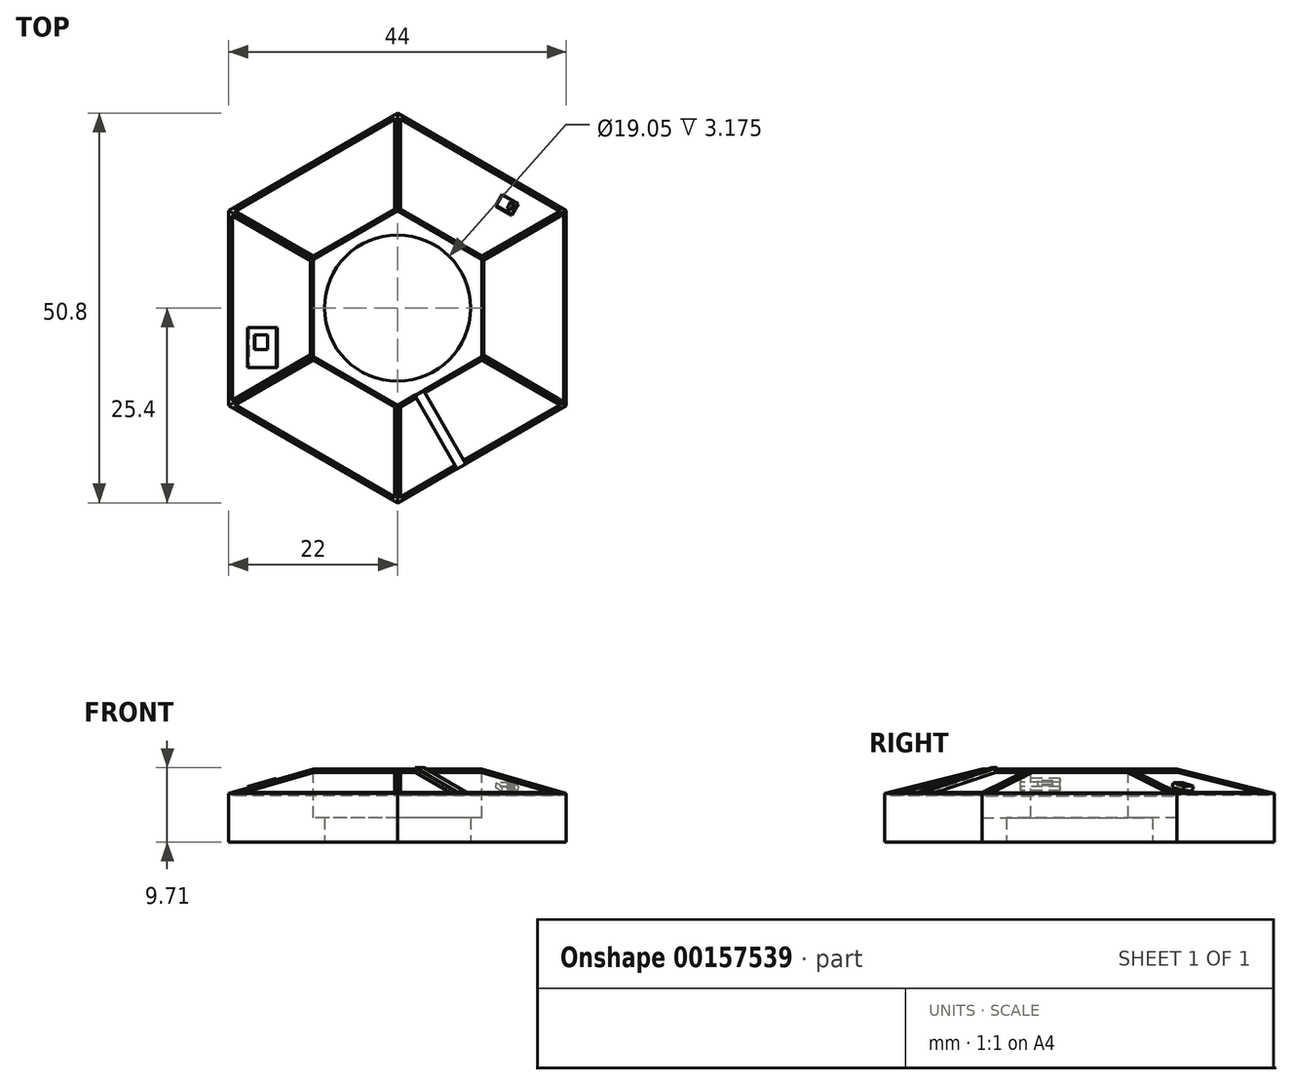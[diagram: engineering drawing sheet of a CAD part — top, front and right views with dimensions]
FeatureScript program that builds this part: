
annotation { "Feature Type Name" : "Feature", "Feature Type Description" : "" }
export const myFeature = defineFeature(function(context is Context, id is Id, definition is map)
    precondition{}
    {
        {
            var Q0;
            Q0=qCreatedBy(makeId("Top.planeOp"),FACE);
            var sketch = newSketch(context, id + "F0", { "sketchPlane" : qUnion([Q0])});
            skCircle(sketch, "E0.cCircle", {"center": v(0, 0) * mm, "radius": 25.4 * mm, "construction": true});
            skLineSegment(sketch, "E0.0", {"start": v(0, 25.4) * mm, "end": v(22, 12.7) * mm});
            skLineSegment(sketch, "E0.1", {"start": v(22, 12.7) * mm, "end": v(22, -12.7) * mm});
            skLineSegment(sketch, "E0.2", {"start": v(22, -12.7) * mm, "end": v(0, -25.4) * mm});
            skLineSegment(sketch, "E0.3", {"start": v(0, -25.4) * mm, "end": v(-22, -12.7) * mm});
            skLineSegment(sketch, "E0.4", {"start": v(-22, -12.7) * mm, "end": v(-22, 12.7) * mm});
            skLineSegment(sketch, "E0.5", {"start": v(-22, 12.7) * mm, "end": v(0, 25.4) * mm});
            skCircle(sketch, "E1.cCircle", {"center": v(0, 0) * mm, "radius": 12.7 * mm, "construction": true});
            skLineSegment(sketch, "E1.0", {"start": v(0, 12.7) * mm, "end": v(11, 6.35) * mm});
            skLineSegment(sketch, "E1.1", {"start": v(11, 6.35) * mm, "end": v(11, -6.35) * mm});
            skLineSegment(sketch, "E1.2", {"start": v(11, -6.35) * mm, "end": v(0, -12.7) * mm});
            skLineSegment(sketch, "E1.3", {"start": v(0, -12.7) * mm, "end": v(-11, -6.35) * mm});
            skLineSegment(sketch, "E1.4", {"start": v(-11, -6.35) * mm, "end": v(-11, 6.35) * mm});
            skLineSegment(sketch, "E1.5", {"start": v(-11, 6.35) * mm, "end": v(0, 12.7) * mm});
            skCircle(sketch, "E2", {"center": v(0, 0) * mm, "radius": 9.53 * mm});
            skSolve(sketch);
        }
        {
            var Q0;
            Q0=makeQuery(id+"F0.imprint","IMPRINT",FACE,{"disambiguationData":[TD([[makeQuery(id+"F0.imprint","IMPRINT",EDGE,{"derivedFrom":sQuery(id+"F0.wireOp",EDGE,"E0.0")}),-1.0]])]});
            var Q1;
            {var subQ0=sQuery(id+"F0.wireOp",EDGE,"Us5ljXmE-I7RQ-zfye-zbqb-6XDtsWbHNBCU");var subQ4=makeQuery(id+"F0.imprint","INTERSECT",VERTEX,{"derivedFrom":[sQuery(id+"F0.wireOp",EDGE,"E1.0"),subQ0]});Q1=makeQuery(id+"F0.imprint","IMPRINT",FACE,{"disambiguationData":[TD([[makeQuery(id+"F0.imprint","IMPRINT",EDGE,{"disambiguationData":[TD([[subQ4,1.0]])],"derivedFrom":subQ0}),1.0]])]});}
            var Q2;
            {var subQ0=sQuery(id+"F0.wireOp",EDGE,"E1.1");var subQ1=sQuery(id+"F0.wireOp",EDGE,"E1.0");var subQ2=makeQuery(id+"F0.imprint","INTERSECT",VERTEX,{"derivedFrom":[subQ1,subQ0]});Q2=makeQuery(id+"F0.imprint","IMPRINT",FACE,{"disambiguationData":[TD([[makeQuery(id+"F0.imprint","IMPRINT",EDGE,{"disambiguationData":[TD([[subQ2,1.0]])],"derivedFrom":subQ1}),-1.0]])]});}
            var Q3;
            {var subQ0=sQuery(id+"F0.wireOp",EDGE,"E1.2");var subQ1=sQuery(id+"F0.wireOp",EDGE,"E1.1");var subQ2=makeQuery(id+"F0.imprint","INTERSECT",VERTEX,{"derivedFrom":[subQ1,subQ0]});Q3=makeQuery(id+"F0.imprint","IMPRINT",FACE,{"disambiguationData":[TD([[makeQuery(id+"F0.imprint","IMPRINT",EDGE,{"disambiguationData":[TD([[subQ2,1.0]])],"derivedFrom":subQ1}),-1.0]])]});}
            var Q4;
            {var subQ0=sQuery(id+"F0.wireOp",EDGE,"E1.3");var subQ1=sQuery(id+"F0.wireOp",EDGE,"E1.2");var subQ2=makeQuery(id+"F0.imprint","INTERSECT",VERTEX,{"derivedFrom":[subQ1,subQ0]});Q4=makeQuery(id+"F0.imprint","IMPRINT",FACE,{"disambiguationData":[TD([[makeQuery(id+"F0.imprint","IMPRINT",EDGE,{"disambiguationData":[TD([[subQ2,1.0]])],"derivedFrom":subQ1}),-1.0]])]});}
            var Q5;
            {var subQ0=sQuery(id+"F0.wireOp",EDGE,"E1.4");var subQ1=sQuery(id+"F0.wireOp",EDGE,"E1.3");var subQ2=makeQuery(id+"F0.imprint","INTERSECT",VERTEX,{"derivedFrom":[subQ1,subQ0]});Q5=makeQuery(id+"F0.imprint","IMPRINT",FACE,{"disambiguationData":[TD([[makeQuery(id+"F0.imprint","IMPRINT",EDGE,{"disambiguationData":[TD([[subQ2,1.0]])],"derivedFrom":subQ1}),-1.0]])]});}
            var Q6;
            {var subQ0=sQuery(id+"F0.wireOp",EDGE,"E1.5");var subQ1=sQuery(id+"F0.wireOp",EDGE,"E1.4");var subQ2=makeQuery(id+"F0.imprint","INTERSECT",VERTEX,{"derivedFrom":[subQ1,subQ0]});Q6=makeQuery(id+"F0.imprint","IMPRINT",FACE,{"disambiguationData":[TD([[makeQuery(id+"F0.imprint","IMPRINT",EDGE,{"disambiguationData":[TD([[subQ2,1.0]])],"derivedFrom":subQ1}),-1.0]])]});}
            var Q7;
            {var subQ0=sQuery(id+"F0.wireOp",EDGE,"E1.5");var subQ1=sQuery(id+"F0.wireOp",EDGE,"E1.0");var subQ2=makeQuery(id+"F0.imprint","INTERSECT",VERTEX,{"derivedFrom":[subQ1,subQ0]});Q7=makeQuery(id+"F0.imprint","IMPRINT",FACE,{"disambiguationData":[TD([[makeQuery(id+"F0.imprint","IMPRINT",EDGE,{"disambiguationData":[TD([[subQ2,-1.0]])],"derivedFrom":subQ1}),-1.0]])]});}
            extrude(context, id + "F1", {"entities" : qUnion([Q0, Q1, Q2, Q3, Q4, Q5, Q6, Q7]), "depth" : 6.35 * mm});
        }
        {
            var Q0;
            Q0=makeQuery(id+"F1.opExtrude","CAP_FACE",FACE,{"disambiguationData":[OSD([sQuery(id+"F0.wireOp",EDGE,"E0.0"),sQuery(id+"F0.wireOp",EDGE,"E0.1"),sQuery(id+"F0.wireOp",EDGE,"E0.2"),sQuery(id+"F0.wireOp",EDGE,"E0.3"),sQuery(id+"F0.wireOp",EDGE,"E0.4"),sQuery(id+"F0.wireOp",EDGE,"E0.5")])],"isStart":false});
            var sketch = newSketch(context, id + "F2", { "sketchPlane" : qUnion([Q0])});
            skLineSegment(sketch, "E3.0", {"start": v(-11, -6.35) * mm, "end": v(-11, 6.35) * mm});
            skLineSegment(sketch, "E3.1", {"start": v(0, -12.7) * mm, "end": v(-11, -6.35) * mm});
            skLineSegment(sketch, "E3.2", {"start": v(11, -6.35) * mm, "end": v(0, -12.7) * mm});
            skLineSegment(sketch, "E3.3", {"start": v(11, 6.35) * mm, "end": v(11, -6.35) * mm});
            skLineSegment(sketch, "E3.4", {"start": v(0, 12.7) * mm, "end": v(11, 6.35) * mm});
            skLineSegment(sketch, "E3.5", {"start": v(-11, 6.35) * mm, "end": v(0, 12.7) * mm});
            skSolve(sketch);
        }
        {
            var Q0;
            Q0=makeQuery(id+"F2.imprint","IMPRINT",FACE,{"disambiguationData":[TD([[makeQuery(id+"F2.imprint","IMPRINT",EDGE,{"derivedFrom":sQuery(id+"F2.wireOp",EDGE,"E3.0")}),-1.0]])]});
            extrude(context, id + "F3", {"entities" : qUnion([Q0]), "operationType" : NewBodyOperationType.ADD, "depth" : 3.17 * mm});
        }
        {
            var Q0;
            Q0=makeQuery(id+"F2.imprint","IMPRINT",FACE,{"disambiguationData":[TD([[makeQuery(id+"F2.imprint","IMPRINT",EDGE,{"derivedFrom":sQuery(id+"F2.wireOp",EDGE,"E3.0")}),1.0]])]});
            var sketch = newSketch(context, id + "F4", { "sketchPlane" : qUnion([Q0])});
            skLineSegment(sketch, "E4.0", {"start": v(22, -12.7) * mm, "end": v(0, -25.4) * mm});
            skLineSegment(sketch, "E4.1", {"start": v(0, -25.4) * mm, "end": v(-22, -12.7) * mm});
            skLineSegment(sketch, "E4.2", {"start": v(-22, -12.7) * mm, "end": v(-22, 12.7) * mm});
            skLineSegment(sketch, "E4.3", {"start": v(-22, 12.7) * mm, "end": v(0, 25.4) * mm});
            skLineSegment(sketch, "E4.4", {"start": v(0, 25.4) * mm, "end": v(22, 12.7) * mm});
            skLineSegment(sketch, "E4.5", {"start": v(22, 12.7) * mm, "end": v(22, -12.7) * mm});
            skSolve(sketch);
        }
        {
            var Q0;
            Q0=makeQuery(id+"F3.opExtrude","CAP_FACE",FACE,{"disambiguationData":[OSD([sQuery(id+"F2.wireOp",EDGE,"E3.0"),sQuery(id+"F2.wireOp",EDGE,"E3.1"),sQuery(id+"F2.wireOp",EDGE,"E3.2"),sQuery(id+"F2.wireOp",EDGE,"E3.3"),sQuery(id+"F2.wireOp",EDGE,"E3.4"),sQuery(id+"F2.wireOp",EDGE,"E3.5")])],"isStart":false});
            var sketch = newSketch(context, id + "F5", { "sketchPlane" : qUnion([Q0])});
            skLineSegment(sketch, "E5.0", {"start": v(11, -6.35) * mm, "end": v(0, -12.7) * mm});
            skLineSegment(sketch, "E5.1", {"start": v(0, -12.7) * mm, "end": v(-11, -6.35) * mm});
            skLineSegment(sketch, "E5.2", {"start": v(-11, -6.35) * mm, "end": v(-11, 6.35) * mm});
            skLineSegment(sketch, "E5.3", {"start": v(-11, 6.35) * mm, "end": v(0, 12.7) * mm});
            skLineSegment(sketch, "E5.4", {"start": v(0, 12.7) * mm, "end": v(11, 6.35) * mm});
            skLineSegment(sketch, "E5.5", {"start": v(11, 6.35) * mm, "end": v(11, -6.35) * mm});
            skSolve(sketch);
        }
        {
            var Q1;
            Q1 = qSketchRegion(id + "F4", true);
            var Q2;
            Q2 = qSketchRegion(id + "F5", true);
            loft(context, id + "F6", {"operationType" : NewBodyOperationType.ADD, "sheetProfilesArray" : [{ "sheetProfileEntities" : qUnion([Q1]) }, { "sheetProfileEntities" : qUnion([Q2]) }]});
        }
        {
            var Q0;
            Q0=makeQuery(id+"F6.opLoft","SWEPT_FACE",FACE,{"disambiguationData":[OSD([sQuery(id+"F4.wireOp",EDGE,"E4.0"),sQuery(id+"F4.wireOp",EDGE,"E4.4"),sQuery(id+"F4.wireOp",EDGE,"E4.5"),sQuery(id+"F5.wireOp",EDGE,"E5.0"),sQuery(id+"F5.wireOp",EDGE,"E5.4"),sQuery(id+"F5.wireOp",EDGE,"E5.5")])]});
            var sketch = newSketch(context, id + "F7", { "sketchPlane" : qUnion([Q0])});
            skLineSegment(sketch, "E6.0.0", {"start": v(19.37, 12.7) * mm, "end": v(7.93, 6.35) * mm});
            skLineSegment(sketch, "E6.0.1", {"start": v(7.93, 6.35) * mm, "end": v(7.93, -6.35) * mm});
            skLineSegment(sketch, "E6.0.2", {"start": v(7.93, -6.35) * mm, "end": v(19.37, -12.7) * mm});
            skLineSegment(sketch, "E6.0.3", {"start": v(19.37, -12.7) * mm, "end": v(19.37, 12.7) * mm});
            skLineSegment(sketch, "E7.0", {"start": v(8.18, -6.2) * mm, "end": v(19.12, -12.27) * mm});
            skLineSegment(sketch, "E7.1", {"start": v(8.18, 6.2) * mm, "end": v(8.18, -6.2) * mm});
            skLineSegment(sketch, "E7.2", {"start": v(19.12, 12.27) * mm, "end": v(8.18, 6.2) * mm});
            skLineSegment(sketch, "E7.3", {"start": v(19.12, -12.27) * mm, "end": v(19.12, 12.27) * mm});
            skSolve(sketch);
        }
        {
            var Q0;
            Q0=makeQuery(id+"F3.opExtrude","CAP_FACE",FACE,{"disambiguationData":[OSD([sQuery(id+"F2.wireOp",EDGE,"E3.0"),sQuery(id+"F2.wireOp",EDGE,"E3.1"),sQuery(id+"F2.wireOp",EDGE,"E3.2"),sQuery(id+"F2.wireOp",EDGE,"E3.3"),sQuery(id+"F2.wireOp",EDGE,"E3.4"),sQuery(id+"F2.wireOp",EDGE,"E3.5")])],"isStart":false});
            var Q1;
            Q1=sQuery(id+"F0.wireOp",EDGE,"E1.3");
            var Q2;
            Q2=sQuery(id+"F0.wireOp",EDGE,"E1.2");
            var Q3;
            Q3=sQuery(id+"F0.wireOp",EDGE,"E1.1");
            var Q4;
            Q4=sQuery(id+"F0.wireOp",EDGE,"E1.0");
            var Q5;
            Q5=sQuery(id+"F0.wireOp",EDGE,"E1.5");
            var Q6;
            Q6=sQuery(id+"F0.wireOp",EDGE,"E1.4");
            extrude(context, id + "F8", {"entities" : qUnion([Q0]), "operationType" : NewBodyOperationType.REMOVE, "surfaceEntities" : qUnion([Q1, Q2, Q3, Q4, Q5, Q6]), "oppositeDirection" : true, "depth" : 6.35 * mm});
        }
        {
            var Q0;
            Q0=makeQuery(id+"F6.opLoft","SWEPT_FACE",FACE,{"disambiguationData":[OSD([sQuery(id+"F4.wireOp",EDGE,"E4.1"),sQuery(id+"F4.wireOp",EDGE,"E4.2"),sQuery(id+"F4.wireOp",EDGE,"E4.3"),sQuery(id+"F5.wireOp",EDGE,"E5.1"),sQuery(id+"F5.wireOp",EDGE,"E5.2"),sQuery(id+"F5.wireOp",EDGE,"E5.3")])]});
            var sketch = newSketch(context, id + "F9", { "sketchPlane" : qUnion([Q0])});
            skLineSegment(sketch, "E8.bottom", {"start": v(-16.76, -2.55) * mm, "end": v(-12.87, -2.55) * mm});
            skLineSegment(sketch, "E8.top", {"start": v(-16.76, -7.73) * mm, "end": v(-12.87, -7.73) * mm});
            skLineSegment(sketch, "E8.left", {"start": v(-16.76, -2.55) * mm, "end": v(-16.76, -7.73) * mm});
            skLineSegment(sketch, "E8.right", {"start": v(-12.87, -2.55) * mm, "end": v(-12.87, -7.73) * mm});
            skLineSegment(sketch, "E9.bottom", {"start": v(-15.8, -3.5) * mm, "end": v(-14.08, -3.5) * mm});
            skLineSegment(sketch, "E9.top", {"start": v(-15.8, -5.4) * mm, "end": v(-14.08, -5.4) * mm});
            skLineSegment(sketch, "E9.left", {"start": v(-15.8, -3.5) * mm, "end": v(-15.8, -5.4) * mm});
            skLineSegment(sketch, "E9.right", {"start": v(-14.08, -3.5) * mm, "end": v(-14.08, -5.4) * mm});
            skSolve(sketch);
        }
        {
            var Q0;
            Q0=makeQuery(id+"F9.imprint","IMPRINT",FACE,{"disambiguationData":[TD([[makeQuery(id+"F9.imprint","IMPRINT",EDGE,{"derivedFrom":sQuery(id+"F9.wireOp",EDGE,"E8.bottom")}),-1.0]])]});
            extrude(context, id + "F10", {"entities" : qUnion([Q0]), "operationType" : NewBodyOperationType.ADD, "depth" : 0.2 * mm});
        }
        {
            var Q0;
            Q0=makeQuery(id+"F6.opLoft","SWEPT_FACE",FACE,{"disambiguationData":[OSD([sQuery(id+"F4.wireOp",EDGE,"E4.0"),sQuery(id+"F4.wireOp",EDGE,"E4.1"),sQuery(id+"F4.wireOp",EDGE,"E4.5"),sQuery(id+"F5.wireOp",EDGE,"E5.0"),sQuery(id+"F5.wireOp",EDGE,"E5.1"),sQuery(id+"F5.wireOp",EDGE,"E5.5")])]});
            var sketch = newSketch(context, id + "F11", { "sketchPlane" : qUnion([Q0])});
            skLineSegment(sketch, "E10", {"start": v(0.55, -8.76) * mm, "end": v(6.1, -18.77) * mm});
            skLineSegment(sketch, "E11", {"start": v(6.1, -18.77) * mm, "end": v(7.28, -18.11) * mm});
            skLineSegment(sketch, "E12", {"start": v(7.28, -18.11) * mm, "end": v(1.73, -8.1) * mm});
            skLineSegment(sketch, "E13", {"start": v(1.73, -8.1) * mm, "end": v(0.55, -8.76) * mm});
            skSolve(sketch);
        }
        {
            var Q0;
            Q0=makeQuery(id+"F11.imprint","IMPRINT",FACE,{"disambiguationData":[TD([[makeQuery(id+"F11.imprint","IMPRINT",EDGE,{"derivedFrom":sQuery(id+"F11.wireOp",EDGE,"E10")}),1.0]])]});
            extrude(context, id + "F12", {"entities" : qUnion([Q0]), "operationType" : NewBodyOperationType.ADD, "depth" : 0.2 * mm});
        }
        {
            var Q0;
            Q0=makeQuery(id+"F7.imprint","IMPRINT",FACE,{"disambiguationData":[TD([[makeQuery(id+"F7.imprint","IMPRINT",EDGE,{"derivedFrom":sQuery(id+"F7.wireOp",EDGE,"E7.0")}),1.0]])]});
            extrude(context, id + "F13", {"entities" : qUnion([Q0]), "operationType" : NewBodyOperationType.REMOVE, "oppositeDirection" : true, "depth" : 0.38 * mm});
        }
        {
            var Q0;
            Q0=makeQuery(id+"F6.opLoft","SWEPT_FACE",FACE,{"disambiguationData":[OSD([sQuery(id+"F4.wireOp",EDGE,"E4.3"),sQuery(id+"F4.wireOp",EDGE,"E4.4"),sQuery(id+"F4.wireOp",EDGE,"E4.5"),sQuery(id+"F5.wireOp",EDGE,"E5.3"),sQuery(id+"F5.wireOp",EDGE,"E5.4"),sQuery(id+"F5.wireOp",EDGE,"E5.5")])]});
            var sketch = newSketch(context, id + "F14", { "sketchPlane" : qUnion([Q0])});
            skLineSegment(sketch, "E14.0", {"start": v(-1.7, 23.1) * mm, "end": v(-1.7, 10.01) * mm});
            skLineSegment(sketch, "E14.1", {"start": v(-1.7, 10.01) * mm, "end": v(9.4, 3.85) * mm});
            skLineSegment(sketch, "E14.2", {"start": v(20.5, 10.78) * mm, "end": v(9.4, 3.85) * mm});
            skLineSegment(sketch, "E14.3", {"start": v(-1.7, 23.1) * mm, "end": v(20.5, 10.78) * mm});
            skLineSegment(sketch, "E15.0", {"start": v(-1.33, 10.24) * mm, "end": v(9.39, 4.3) * mm});
            skLineSegment(sketch, "E15.1", {"start": v(-1.33, 22.45) * mm, "end": v(-1.33, 10.24) * mm});
            skLineSegment(sketch, "E15.2", {"start": v(-1.33, 22.45) * mm, "end": v(19.75, 10.76) * mm});
            skLineSegment(sketch, "E15.3", {"start": v(19.75, 10.76) * mm, "end": v(9.39, 4.3) * mm});
            skSolve(sketch);
        }
        {
            var Q0;
            Q0=makeQuery(id+"F14.imprint","IMPRINT",FACE,{"disambiguationData":[TD([[makeQuery(id+"F14.imprint","IMPRINT",EDGE,{"derivedFrom":sQuery(id+"F14.wireOp",EDGE,"E15.0")}),1.0]])]});
            extrude(context, id + "F15", {"entities" : qUnion([Q0]), "operationType" : NewBodyOperationType.REMOVE, "oppositeDirection" : true, "depth" : 0.38 * mm});
        }
        {
            var Q0;
            Q0=makeQuery(id+"F6.opLoft","SWEPT_FACE",FACE,{"disambiguationData":[OSD([sQuery(id+"F4.wireOp",EDGE,"E4.2"),sQuery(id+"F4.wireOp",EDGE,"E4.3"),sQuery(id+"F4.wireOp",EDGE,"E4.4"),sQuery(id+"F5.wireOp",EDGE,"E5.2"),sQuery(id+"F5.wireOp",EDGE,"E5.3"),sQuery(id+"F5.wireOp",EDGE,"E5.4")])]});
            var sketch = newSketch(context, id + "F16", { "sketchPlane" : qUnion([Q0])});
            skLineSegment(sketch, "E16.0", {"start": v(-9.4, 3.85) * mm, "end": v(1.7, 10.01) * mm});
            skLineSegment(sketch, "E16.1", {"start": v(1.7, 23.1) * mm, "end": v(1.7, 10.01) * mm});
            skLineSegment(sketch, "E16.2", {"start": v(-20.5, 10.78) * mm, "end": v(1.7, 23.1) * mm});
            skLineSegment(sketch, "E16.3", {"start": v(-20.5, 10.78) * mm, "end": v(-9.4, 3.85) * mm});
            skLineSegment(sketch, "E17.0", {"start": v(-9.39, 4.3) * mm, "end": v(1.33, 10.24) * mm});
            skLineSegment(sketch, "E17.1", {"start": v(-19.75, 10.76) * mm, "end": v(-9.39, 4.3) * mm});
            skLineSegment(sketch, "E17.2", {"start": v(-19.75, 10.76) * mm, "end": v(1.33, 22.45) * mm});
            skLineSegment(sketch, "E17.3", {"start": v(1.33, 22.45) * mm, "end": v(1.33, 10.24) * mm});
            skSolve(sketch);
        }
        {
            var Q0;
            Q0=makeQuery(id+"F16.imprint","IMPRINT",FACE,{"disambiguationData":[TD([[makeQuery(id+"F16.imprint","IMPRINT",EDGE,{"derivedFrom":sQuery(id+"F16.wireOp",EDGE,"E17.0")}),1.0]])]});
            extrude(context, id + "F17", {"entities" : qUnion([Q0]), "operationType" : NewBodyOperationType.REMOVE, "oppositeDirection" : true, "depth" : 0.38 * mm});
        }
        {
            var Q0;
            {var subQ1=sQuery(id+"F5.wireOp",EDGE,"E5.3");var subQ2=sQuery(id+"F5.wireOp",EDGE,"E5.2");var subQ3=sQuery(id+"F5.wireOp",EDGE,"E5.1");var subQ5=sQuery(id+"F4.wireOp",EDGE,"E4.2");var subQ6=sQuery(id+"F4.wireOp",EDGE,"E4.1");var subQ7=sQuery(id+"F4.wireOp",EDGE,"E4.3");Q0=makeQuery(id+"F10.boolean.opBoolean","SPLIT",FACE,{"disambiguationData":[TD([makeQuery(id+"F1.opExtrude","SWEPT_FACE",FACE,{"disambiguationData":[OSD([sQuery(id+"F0.wireOp",EDGE,"E0.3")])]})])],"derivedFrom":makeQuery(id+"F6.opLoft","SWEPT_FACE",FACE,{"disambiguationData":[OSD([subQ6,subQ5,subQ7,subQ3,subQ2,subQ1])]})});}
            var sketch = newSketch(context, id + "F18", { "sketchPlane" : qUnion([Q0])});
            skLineSegment(sketch, "E18.0", {"start": v(-19.37, 12.7) * mm, "end": v(-7.93, 6.35) * mm});
            skLineSegment(sketch, "E18.1", {"start": v(-7.93, -6.35) * mm, "end": v(-7.93, 6.35) * mm});
            skLineSegment(sketch, "E18.2", {"start": v(-19.37, -12.7) * mm, "end": v(-7.93, -6.35) * mm});
            skLineSegment(sketch, "E18.3", {"start": v(-19.37, -12.7) * mm, "end": v(-19.37, 12.7) * mm});
            skLineSegment(sketch, "E18.4", {"start": v(-16.76, -2.55) * mm, "end": v(-16.76, -7.73) * mm});
            skLineSegment(sketch, "E18.5", {"start": v(-16.76, -2.55) * mm, "end": v(-12.87, -2.55) * mm});
            skLineSegment(sketch, "E18.6", {"start": v(-12.87, -2.55) * mm, "end": v(-12.87, -7.73) * mm});
            skLineSegment(sketch, "E18.7", {"start": v(-16.76, -7.73) * mm, "end": v(-12.87, -7.73) * mm});
            skLineSegment(sketch, "E19.0", {"start": v(-19, 12.05) * mm, "end": v(-8.3, 6.13) * mm});
            skLineSegment(sketch, "E19.1", {"start": v(-19, -12.05) * mm, "end": v(-19, 12.05) * mm});
            skLineSegment(sketch, "E19.2", {"start": v(-19, -12.05) * mm, "end": v(-8.3, -6.13) * mm});
            skLineSegment(sketch, "E19.3", {"start": v(-8.3, -6.13) * mm, "end": v(-8.3, 6.13) * mm});
            skSolve(sketch);
        }
        {
            var Q0;
            Q0=makeQuery(id+"F18.imprint","IMPRINT",FACE,{"disambiguationData":[TD([[makeQuery(id+"F18.imprint","IMPRINT",EDGE,{"derivedFrom":sQuery(id+"F18.wireOp",EDGE,"E18.4")}),-1.0]])]});
            extrude(context, id + "F19", {"entities" : qUnion([Q0]), "operationType" : NewBodyOperationType.REMOVE, "oppositeDirection" : true, "depth" : 0.38 * mm});
        }
        {
            var Q0;
            Q0=makeQuery(id+"F6.opLoft","SWEPT_FACE",FACE,{"disambiguationData":[OSD([sQuery(id+"F4.wireOp",EDGE,"E4.0"),sQuery(id+"F4.wireOp",EDGE,"E4.1"),sQuery(id+"F4.wireOp",EDGE,"E4.2"),sQuery(id+"F5.wireOp",EDGE,"E5.0"),sQuery(id+"F5.wireOp",EDGE,"E5.1"),sQuery(id+"F5.wireOp",EDGE,"E5.2")])]});
            var sketch = newSketch(context, id + "F20", { "sketchPlane" : qUnion([Q0])});
            skLineSegment(sketch, "E20.0", {"start": v(1.7, -10.01) * mm, "end": v(-9.4, -3.85) * mm});
            skLineSegment(sketch, "E20.1", {"start": v(1.7, -23.1) * mm, "end": v(1.7, -10.01) * mm});
            skLineSegment(sketch, "E20.2", {"start": v(1.7, -23.1) * mm, "end": v(-20.5, -10.78) * mm});
            skLineSegment(sketch, "E20.3", {"start": v(-20.5, -10.78) * mm, "end": v(-9.4, -3.85) * mm});
            skLineSegment(sketch, "E21.0", {"start": v(1.33, -10.24) * mm, "end": v(-9.39, -4.3) * mm});
            skLineSegment(sketch, "E21.1", {"start": v(1.33, -22.45) * mm, "end": v(1.33, -10.24) * mm});
            skLineSegment(sketch, "E21.2", {"start": v(1.33, -22.45) * mm, "end": v(-19.75, -10.76) * mm});
            skLineSegment(sketch, "E21.3", {"start": v(-19.75, -10.76) * mm, "end": v(-9.39, -4.3) * mm});
            skSolve(sketch);
        }
        {
            var Q0;
            Q0=makeQuery(id+"F20.imprint","IMPRINT",FACE,{"disambiguationData":[TD([[makeQuery(id+"F20.imprint","IMPRINT",EDGE,{"derivedFrom":sQuery(id+"F20.wireOp",EDGE,"E21.0")}),1.0]])]});
            extrude(context, id + "F21", {"entities" : qUnion([Q0]), "operationType" : NewBodyOperationType.REMOVE, "oppositeDirection" : true, "depth" : 0.38 * mm});
        }
        {
            var Q0;
            {var subQ1=sQuery(id+"F5.wireOp",EDGE,"E5.1");var subQ2=sQuery(id+"F5.wireOp",EDGE,"E5.0");var subQ3=sQuery(id+"F4.wireOp",EDGE,"E4.1");var subQ4=sQuery(id+"F4.wireOp",EDGE,"E4.0");var subQ5=sQuery(id+"F5.wireOp",EDGE,"E5.5");Q0=makeQuery(id+"F12.boolean.opBoolean","SPLIT",FACE,{"disambiguationData":[TD([makeQuery(id+"F1.opExtrude","SWEPT_FACE",FACE,{"disambiguationData":[OSD([sQuery(id+"F0.wireOp",EDGE,"E0.3")])]})])],"derivedFrom":makeQuery(id+"F6.opLoft","SWEPT_FACE",FACE,{"disambiguationData":[OSD([subQ4,subQ3,sQuery(id+"F4.wireOp",EDGE,"E4.5"),subQ2,subQ1,subQ5])]})});}
            var sketch = newSketch(context, id + "F22", { "sketchPlane" : qUnion([Q0])});
            skLineSegment(sketch, "E22.0", {"start": v(0.55, -8.76) * mm, "end": v(-1.7, -10.01) * mm});
            skLineSegment(sketch, "E22.1", {"start": v(-1.7, -23.1) * mm, "end": v(-1.7, -10.01) * mm});
            skLineSegment(sketch, "E22.2", {"start": v(6.1, -18.77) * mm, "end": v(-1.7, -23.1) * mm});
            skLineSegment(sketch, "E22.3", {"start": v(20.5, -10.78) * mm, "end": v(7.28, -18.11) * mm});
            skLineSegment(sketch, "E22.4", {"start": v(20.5, -10.78) * mm, "end": v(9.4, -3.85) * mm});
            skLineSegment(sketch, "E22.5", {"start": v(9.4, -3.85) * mm, "end": v(1.73, -8.1) * mm});
            skLineSegment(sketch, "E23.0", {"start": v(19.75, -10.76) * mm, "end": v(9.39, -4.3) * mm});
            skLineSegment(sketch, "E23.1", {"start": v(19.75, -10.76) * mm, "end": v(7.1, -17.78) * mm});
            skLineSegment(sketch, "E23.2", {"start": v(9.39, -4.3) * mm, "end": v(1.92, -8.44) * mm});
            skLineSegment(sketch, "E23.3", {"start": v(7.1, -17.78) * mm, "end": v(5.92, -18.43) * mm});
            skLineSegment(sketch, "E23.4", {"start": v(1.92, -8.44) * mm, "end": v(0.74, -9.1) * mm});
            skLineSegment(sketch, "E23.5", {"start": v(0.74, -9.1) * mm, "end": v(-1.33, -10.24) * mm});
            skLineSegment(sketch, "E23.6", {"start": v(-1.33, -22.45) * mm, "end": v(-1.33, -10.24) * mm});
            skLineSegment(sketch, "E23.7", {"start": v(5.92, -18.43) * mm, "end": v(-1.33, -22.45) * mm});
            skLineSegment(sketch, "E24.0", {"start": v(7.28, -18.11) * mm, "end": v(1.73, -8.1) * mm});
            skLineSegment(sketch, "E24.1", {"start": v(0.55, -8.76) * mm, "end": v(6.1, -18.77) * mm});
            skSolve(sketch);
        }
        {
            var Q0;
            Q0=makeQuery(id+"F22.imprint","IMPRINT",FACE,{"disambiguationData":[TD([[makeQuery(id+"F22.imprint","IMPRINT",EDGE,{"derivedFrom":sQuery(id+"F22.wireOp",EDGE,"E23.0")}),1.0]])]});
            var Q1;
            {var subQ0=sQuery(id+"F22.wireOp",EDGE,"E23.5");Q1=makeQuery(id+"F22.imprint","IMPRINT",FACE,{"disambiguationData":[TD([[makeQuery(id+"F22.imprint","IMPRINT",EDGE,{"derivedFrom":subQ0}),1.0]])]});}
            extrude(context, id + "F23", {"entities" : qUnion([Q0, Q1]), "operationType" : NewBodyOperationType.REMOVE, "oppositeDirection" : true, "depth" : 0.38 * mm});
        }
        {
            var Q0;
            Q0=makeQuery(id+"F15.boolean.opBoolean","COPY",FACE,{"derivedFrom":makeQuery(id+"F15.opExtrude","CAP_FACE",FACE,{"disambiguationData":[OSD([sQuery(id+"F14.wireOp",EDGE,"E15.0"),sQuery(id+"F14.wireOp",EDGE,"E15.1"),sQuery(id+"F14.wireOp",EDGE,"E15.2"),sQuery(id+"F14.wireOp",EDGE,"E15.3")])],"isStart":false})});
            var sketch = newSketch(context, id + "F24", { "sketchPlane" : qUnion([Q0])});
            skLineSegment(sketch, "E25", {"start": v(9.21, 16.6) * mm, "end": v(4.03, 7.26) * mm});
            skLineSegment(sketch, "E26", {"start": v(8.17, 14.74) * mm, "end": v(14.15, 11.42) * mm});
            skLineSegment(sketch, "E27", {"start": v(14.15, 11.42) * mm, "end": v(13.34, 9.96) * mm});
            skLineSegment(sketch, "E28", {"start": v(13.34, 9.96) * mm, "end": v(11.23, 11.13) * mm});
            skLineSegment(sketch, "E29", {"start": v(11.23, 11.13) * mm, "end": v(12.04, 12.6) * mm});
            skLineSegment(sketch, "E30", {"start": v(8.04, 14.49) * mm, "end": v(13.62, 11.39) * mm});
            skLineSegment(sketch, "E31", {"start": v(13.62, 11.39) * mm, "end": v(13.15, 10.54) * mm});
            skLineSegment(sketch, "E32", {"start": v(13.15, 10.54) * mm, "end": v(12.69, 10.8) * mm});
            skLineSegment(sketch, "E33", {"start": v(12.69, 10.8) * mm, "end": v(13.16, 11.64) * mm});
            skSolve(sketch);
        }
        {
            var Q0;
            {var subQ6=sQuery(id+"F24.wireOp",EDGE,"E27");Q0=makeQuery(id+"F24.imprint","IMPRINT",FACE,{"disambiguationData":[TD([[makeQuery(id+"F24.imprint","IMPRINT",EDGE,{"derivedFrom":subQ6}),-1.0]])]});}
            extrude(context, id + "F25", {"entities" : qUnion([Q0]), "operationType" : NewBodyOperationType.ADD, "depth" : 0.64 * mm});
        }
    });
